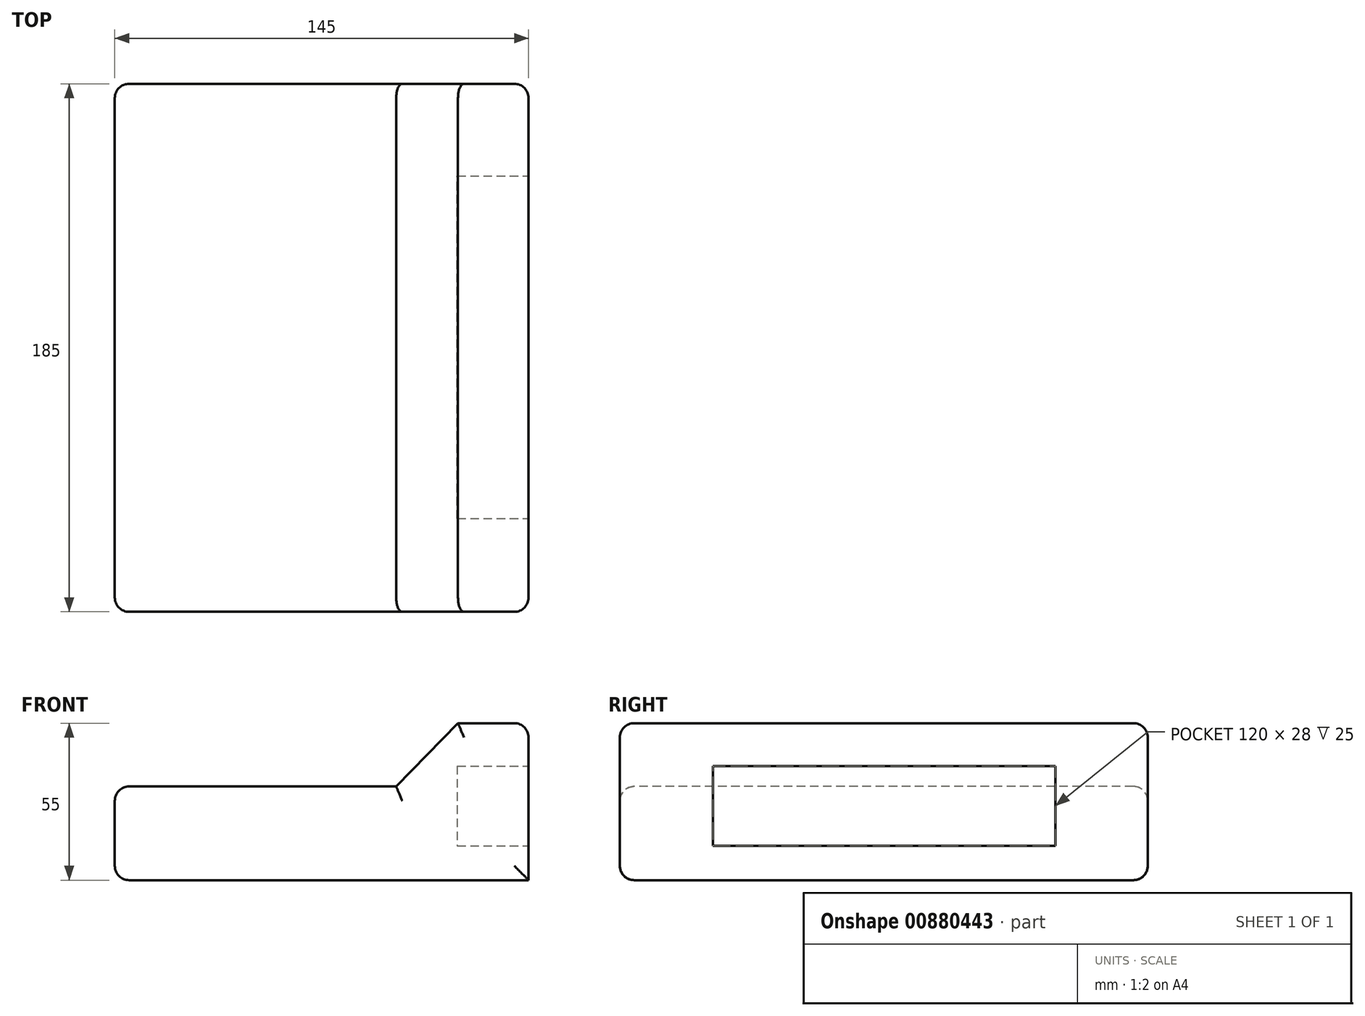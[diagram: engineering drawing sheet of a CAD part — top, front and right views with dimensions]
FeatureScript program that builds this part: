
annotation { "Feature Type Name" : "Feature", "Feature Type Description" : "" }
export const myFeature = defineFeature(function(context is Context, id is Id, definition is map)
    precondition{}
    {
        {
            var Q0;
            Q0=qCreatedBy(makeId("Top.planeOp"),FACE);
            var sketch = newSketch(context, id + "F0", { "sketchPlane" : qUnion([Q0])});
            skLineSegment(sketch, "E0.bottom", {"start": v(72.5, -92.5) * mm, "end": v(-72.5, -92.5) * mm});
            skLineSegment(sketch, "E0.top", {"start": v(72.5, 92.5) * mm, "end": v(-72.5, 92.5) * mm});
            skLineSegment(sketch, "E0.left", {"start": v(72.5, -92.5) * mm, "end": v(72.5, 92.5) * mm});
            skLineSegment(sketch, "E0.right", {"start": v(-72.5, -92.5) * mm, "end": v(-72.5, 92.5) * mm});
            skPoint(sketch, "E0.middle", {"position": v(0, 0) * mm});
            skSolve(sketch);
        }
        {
            var Q0;
            Q0 = qSketchRegion(id + "F0", true);
            extrude(context, id + "F1", {"entities" : qUnion([Q0]), "depth" : 55 * mm, "offsetDistance" : 25 * mm});
        }
        {
            var Q0;
            Q0=qCreatedBy(makeId("Front.planeOp"),FACE);
            var sketch = newSketch(context, id + "F2", { "sketchPlane" : qUnion([Q0])});
            skLineSegment(sketch, "E1", {"start": v(-92.8, 32.82) * mm, "end": v(26.11, 32.82) * mm});
            skLineSegment(sketch, "E2", {"start": v(26.11, 32.82) * mm, "end": v(47.77, 55) * mm});
            skLineSegment(sketch, "E3", {"start": v(47.77, 55) * mm, "end": v(-92.57, 55) * mm});
            skLineSegment(sketch, "E4", {"start": v(-92.57, 55) * mm, "end": v(-92.8, 32.82) * mm});
            skSolve(sketch);
        }
        {
            var Q0;
            Q0 = qSketchRegion(id + "F2", true);
            extrude(context, id + "F3", {"entities" : qUnion([Q0]), "operationType" : NewBodyOperationType.REMOVE, "endBound" : BoundingType.SYMMETRIC, "oppositeDirection" : true, "depth" : 196 * mm, "offsetDistance" : 25 * mm});
        }
        {
            var Q0;
            Q0=makeQuery(id+"F1.opExtrude","SWEPT_FACE",FACE,{"disambiguationData":[OSD([sQuery(id+"F0.wireOp",EDGE,"E0.left")])]});
            var sketch = newSketch(context, id + "F4", { "sketchPlane" : qUnion([Q0])});
            skLineSegment(sketch, "E5", {"start": v(-111.41, 16.68) * mm, "end": v(118.63, 16.68) * mm, "construction": true});
            skSolve(sketch);
        }
        {
            var Q0;
            {var subQ0=sQuery(id+"F0.wireOp",EDGE,"E0.left");Q0=makeQuery(id+"F4.imprint","IMPRINT",FACE,{"disambiguationData":[TD([[makeQuery(id+"F4.imprint","IMPRINT",EDGE,{"derivedFrom":makeQuery(id+"F1.opExtrude","CAP_EDGE",EDGE,{"disambiguationData":[OSD([subQ0])],"isStart":true})}),1.0]])]});}
            var sketch = newSketch(context, id + "F5", { "sketchPlane" : qUnion([Q0])});
            skLineSegment(sketch, "E6.bottom", {"start": v(-59.83, 40) * mm, "end": v(60.17, 40) * mm});
            skLineSegment(sketch, "E6.top", {"start": v(-59.83, 12) * mm, "end": v(60.17, 12) * mm});
            skLineSegment(sketch, "E6.left", {"start": v(-59.83, 40) * mm, "end": v(-59.83, 12) * mm});
            skLineSegment(sketch, "E6.right", {"start": v(60.17, 40) * mm, "end": v(60.17, 12) * mm});
            skSolve(sketch);
        }
        {
            var Q0;
            Q0 = qSketchRegion(id + "F5", true);
            extrude(context, id + "F6", {"entities" : qUnion([Q0]), "operationType" : NewBodyOperationType.REMOVE, "oppositeDirection" : true, "depth" : 25 * mm, "offsetDistance" : 25 * mm});
        }
        {
            var Q0;
            Q0=makeQuery(id+"F3.boolean.opBoolean","INTERSECT",EDGE,{"derivedFrom":[makeQuery(id+"F1.opExtrude","SWEPT_FACE",FACE,{"disambiguationData":[OSD([sQuery(id+"F0.wireOp",EDGE,"E0.bottom")])]}),makeQuery(id+"F3.opExtrude","SWEPT_FACE",FACE,{"disambiguationData":[OSD([sQuery(id+"F2.wireOp",EDGE,"E1")])]})]});
            var Q1;
            Q1=makeQuery(id+"F3.boolean.opBoolean","INTERSECT",EDGE,{"derivedFrom":[makeQuery(id+"F1.opExtrude","SWEPT_FACE",FACE,{"disambiguationData":[OSD([sQuery(id+"F0.wireOp",EDGE,"E0.bottom")])]}),makeQuery(id+"F3.opExtrude","SWEPT_FACE",FACE,{"disambiguationData":[OSD([sQuery(id+"F2.wireOp",EDGE,"E2")])]})]});
            var Q2;
            Q2=makeQuery(id+"F3.boolean.opBoolean","INTERSECT",EDGE,{"derivedFrom":[makeQuery(id+"F1.opExtrude","SWEPT_FACE",FACE,{"disambiguationData":[OSD([sQuery(id+"F0.wireOp",EDGE,"E0.right")])]}),makeQuery(id+"F3.opExtrude","SWEPT_FACE",FACE,{"disambiguationData":[OSD([sQuery(id+"F2.wireOp",EDGE,"E1")])]})]});
            var Q3;
            Q3=makeQuery(id+"F3.boolean.opBoolean","INTERSECT",EDGE,{"derivedFrom":[makeQuery(id+"F1.opExtrude","SWEPT_FACE",FACE,{"disambiguationData":[OSD([sQuery(id+"F0.wireOp",EDGE,"E0.top")])]}),makeQuery(id+"F3.opExtrude","SWEPT_FACE",FACE,{"disambiguationData":[OSD([sQuery(id+"F2.wireOp",EDGE,"E1")])]})]});
            var Q4;
            Q4=makeQuery(id+"F3.boolean.opBoolean","INTERSECT",EDGE,{"derivedFrom":[makeQuery(id+"F1.opExtrude","SWEPT_FACE",FACE,{"disambiguationData":[OSD([sQuery(id+"F0.wireOp",EDGE,"E0.top")])]}),makeQuery(id+"F3.opExtrude","SWEPT_FACE",FACE,{"disambiguationData":[OSD([sQuery(id+"F2.wireOp",EDGE,"E2")])]})]});
            var Q5;
            Q5=makeQuery(id+"F3.boolean.opBoolean","COPY",EDGE,{"derivedFrom":makeQuery(id+"F3.opExtrude","SWEPT_EDGE",EDGE,{"disambiguationData":[OSD([sQuery(id+"F2.wireOp",EDGE,"E2"),sQuery(id+"F2.wireOp",EDGE,"E3")])]})});
            var Q6;
            Q6=makeQuery(id+"F1.opExtrude","CAP_EDGE",EDGE,{"disambiguationData":[OSD([sQuery(id+"F0.wireOp",EDGE,"E0.left")])],"isStart":false});
            var Q7;
            Q7=makeQuery(id+"F1.opExtrude","CAP_EDGE",EDGE,{"disambiguationData":[OSD([sQuery(id+"F0.wireOp",EDGE,"E0.bottom")])],"isStart":false});
            var Q8;
            Q8=makeQuery(id+"F1.opExtrude","SWEPT_EDGE",EDGE,{"disambiguationData":[OSD([sQuery(id+"F0.wireOp",EDGE,"E0.bottom"),sQuery(id+"F0.wireOp",EDGE,"E0.left")])]});
            var Q9;
            Q9=makeQuery(id+"F1.opExtrude","SWEPT_EDGE",EDGE,{"disambiguationData":[OSD([sQuery(id+"F0.wireOp",EDGE,"E0.top"),sQuery(id+"F0.wireOp",EDGE,"E0.left")])]});
            var Q10;
            Q10=makeQuery(id+"F1.opExtrude","CAP_EDGE",EDGE,{"disambiguationData":[OSD([sQuery(id+"F0.wireOp",EDGE,"E0.top")])],"isStart":false});
            var Q11;
            Q11=makeQuery(id+"F1.opExtrude","CAP_EDGE",EDGE,{"disambiguationData":[OSD([sQuery(id+"F0.wireOp",EDGE,"E0.bottom")])],"isStart":true});
            var Q12;
            Q12=makeQuery(id+"F1.opExtrude","CAP_EDGE",EDGE,{"disambiguationData":[OSD([sQuery(id+"F0.wireOp",EDGE,"E0.top")])],"isStart":true});
            var Q13;
            Q13=makeQuery(id+"F1.opExtrude","SWEPT_FACE",FACE,{"disambiguationData":[OSD([sQuery(id+"F0.wireOp",EDGE,"E0.right")])]});
            fillet(context, id + "F7", {"entities" : qUnion([Q0, Q1, Q2, Q3, Q4, Q5, Q6, Q7, Q8, Q9, Q10, Q11, Q12, Q13]), "radius" : 5 * mm, "tangentPropagation" : true, "allowEdgeOverflow" : false});
        }
    });
